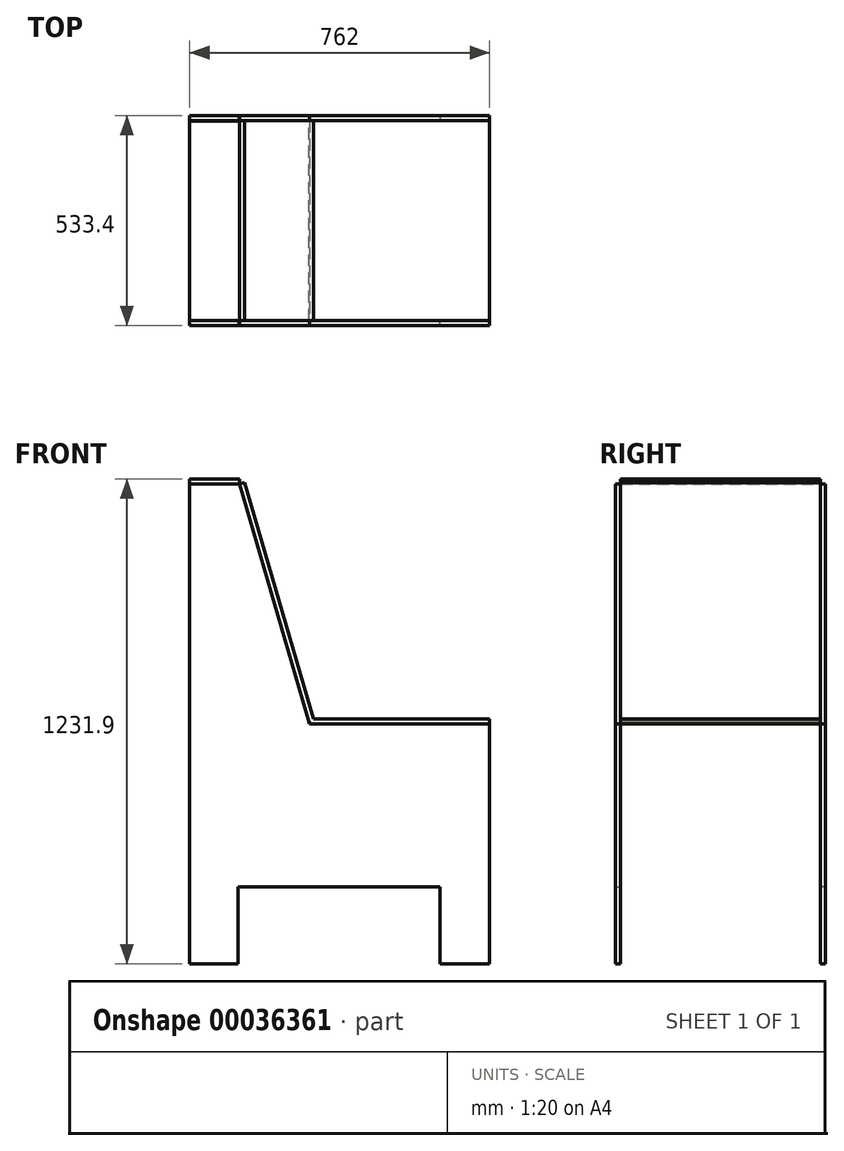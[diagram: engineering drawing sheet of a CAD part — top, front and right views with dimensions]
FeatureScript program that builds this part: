
annotation { "Feature Type Name" : "Feature", "Feature Type Description" : "" }
export const myFeature = defineFeature(function(context is Context, id is Id, definition is map)
    precondition{}
    {
        {
            var Q0;
            Q0=qCreatedBy(makeId("Front.planeOp"),FACE);
            var sketch = newSketch(context, id + "F0", { "sketchPlane" : qUnion([Q0])});
            skLineSegment(sketch, "E0", {"start": v(98.48, 576.75) * mm, "end": v(98.48, -642.45) * mm});
            skLineSegment(sketch, "E1", {"start": v(98.48, 576.75) * mm, "end": v(225.48, 576.75) * mm});
            skLineSegment(sketch, "E2", {"start": v(225.48, 576.75) * mm, "end": v(403.28, -32.85) * mm});
            skLineSegment(sketch, "E3", {"start": v(403.28, -32.85) * mm, "end": v(860.48, -32.85) * mm});
            skLineSegment(sketch, "E4", {"start": v(98.48, -642.45) * mm, "end": v(860.48, -642.45) * mm});
            skLineSegment(sketch, "E5", {"start": v(860.48, -32.85) * mm, "end": v(860.48, -642.45) * mm});
            skSolve(sketch);
        }
        {
            var Q0;
            Q0=makeQuery(id+"F0.imprint","IMPRINT",FACE,{"disambiguationData":[TD([[makeQuery(id+"F0.imprint","IMPRINT",EDGE,{"derivedFrom":sQuery(id+"F0.wireOp",EDGE,"E0")}),1.0]])]});
            extrude(context, id + "F1", {"entities" : qUnion([Q0]), "oppositeDirection" : true, "depth" : 12.7 * mm});
        }
        {
            var Q0;
            Q0=makeQuery(id+"F1.opExtrude","CAP_FACE",FACE,{"disambiguationData":[OSD([sQuery(id+"F0.wireOp",EDGE,"E0"),sQuery(id+"F0.wireOp",EDGE,"E1"),sQuery(id+"F0.wireOp",EDGE,"E2"),sQuery(id+"F0.wireOp",EDGE,"E3"),sQuery(id+"F0.wireOp",EDGE,"E4"),sQuery(id+"F0.wireOp",EDGE,"E5")])],"isStart":true});
            var sketch = newSketch(context, id + "F2", { "sketchPlane" : qUnion([Q0])});
            skLineSegment(sketch, "E6.bottom", {"start": v(221.16, -446.46) * mm, "end": v(733.7, -446.46) * mm});
            skLineSegment(sketch, "E6.top", {"start": v(221.16, -642.45) * mm, "end": v(733.7, -642.45) * mm});
            skLineSegment(sketch, "E6.left", {"start": v(221.16, -446.46) * mm, "end": v(221.16, -642.45) * mm});
            skLineSegment(sketch, "E6.right", {"start": v(733.7, -446.46) * mm, "end": v(733.7, -642.45) * mm});
            skSolve(sketch);
        }
        {
            var Q0;
            Q0=makeQuery(id+"F2.imprint","IMPRINT",FACE,{"disambiguationData":[TD([[makeQuery(id+"F2.imprint","IMPRINT",EDGE,{"derivedFrom":sQuery(id+"F2.wireOp",EDGE,"E6.bottom")}),-1.0]])]});
            extrude(context, id + "F3", {"entities" : qUnion([Q0]), "operationType" : NewBodyOperationType.REMOVE, "endBound" : BoundingType.THROUGH_ALL, "oppositeDirection" : true, "depth" : 12.7 * mm});
        }
        {
            var Q0;
            Q0=makeQuery(id+"F1.opExtrude","CAP_FACE",FACE,{"disambiguationData":[OSD([sQuery(id+"F0.wireOp",EDGE,"E0"),sQuery(id+"F0.wireOp",EDGE,"E1"),sQuery(id+"F0.wireOp",EDGE,"E2"),sQuery(id+"F0.wireOp",EDGE,"E3"),sQuery(id+"F0.wireOp",EDGE,"E4"),sQuery(id+"F0.wireOp",EDGE,"E5")])],"isStart":true});
            var sketch = newSketch(context, id + "F4", { "sketchPlane" : qUnion([Q0])});
            skLineSegment(sketch, "E7.0", {"start": v(98.48, 576.75) * mm, "end": v(225.48, 576.75) * mm});
            skLineSegment(sketch, "E8.0", {"start": v(225.48, 576.75) * mm, "end": v(403.28, -32.85) * mm});
            skLineSegment(sketch, "E9.0", {"start": v(403.28, -32.85) * mm, "end": v(860.48, -32.85) * mm});
            skLineSegment(sketch, "E10.0", {"start": v(860.48, -32.85) * mm, "end": v(860.48, -642.45) * mm});
            skLineSegment(sketch, "E11.0", {"start": v(733.7, -642.45) * mm, "end": v(860.48, -642.45) * mm});
            skLineSegment(sketch, "E12.0", {"start": v(733.7, -446.46) * mm, "end": v(733.7, -642.45) * mm});
            skLineSegment(sketch, "E13.0", {"start": v(221.16, -446.46) * mm, "end": v(733.7, -446.46) * mm});
            skLineSegment(sketch, "E14.0", {"start": v(221.16, -446.46) * mm, "end": v(221.16, -642.45) * mm});
            skLineSegment(sketch, "E15.0", {"start": v(98.48, -642.45) * mm, "end": v(221.16, -642.45) * mm});
            skLineSegment(sketch, "E16.0", {"start": v(98.48, 576.75) * mm, "end": v(98.48, -642.45) * mm});
            skSolve(sketch);
        }
        {
            var Q0;
            Q0=makeQuery(id+"F4.imprint","IMPRINT",FACE,{"disambiguationData":[TD([[makeQuery(id+"F4.imprint","IMPRINT",EDGE,{"derivedFrom":sQuery(id+"F4.wireOp",EDGE,"E7.0")}),-1.0]])]});
            cPlane(context, id + "F5", {"entities" : qUnion([Q0]), "cplaneType" : CPlaneType.OFFSET, "offset" : 508 * mm, "width" : 152.4 * mm, "height" : 152.4 * mm});
        }
        {
            var Q0;
            Q0=qCreatedBy(id+"F5.planeOp",FACE);
            var sketch = newSketch(context, id + "F6", { "sketchPlane" : qUnion([Q0])});
            skLineSegment(sketch, "E17.0", {"start": v(225.48, 576.75) * mm, "end": v(403.28, -32.85) * mm});
            skLineSegment(sketch, "E18.0", {"start": v(403.28, -32.85) * mm, "end": v(860.48, -32.85) * mm});
            skLineSegment(sketch, "E19.0", {"start": v(860.48, -32.85) * mm, "end": v(860.48, -642.45) * mm});
            skLineSegment(sketch, "E20.0", {"start": v(733.7, -642.45) * mm, "end": v(860.48, -642.45) * mm});
            skLineSegment(sketch, "E21.0", {"start": v(733.7, -446.46) * mm, "end": v(733.7, -642.45) * mm});
            skLineSegment(sketch, "E22.0", {"start": v(221.16, -446.46) * mm, "end": v(733.7, -446.46) * mm});
            skLineSegment(sketch, "E23.0", {"start": v(221.16, -446.46) * mm, "end": v(221.16, -642.45) * mm});
            skLineSegment(sketch, "E24.0", {"start": v(98.48, -642.45) * mm, "end": v(221.16, -642.45) * mm});
            skLineSegment(sketch, "E25.0", {"start": v(98.48, 576.75) * mm, "end": v(98.48, -642.45) * mm});
            skLineSegment(sketch, "E26.0", {"start": v(98.48, 576.75) * mm, "end": v(225.48, 576.75) * mm});
            skSolve(sketch);
        }
        {
            var Q0;
            Q0=makeQuery(id+"F6.imprint","IMPRINT",FACE,{"disambiguationData":[TD([[makeQuery(id+"F6.imprint","IMPRINT",EDGE,{"derivedFrom":sQuery(id+"F6.wireOp",EDGE,"E17.0")}),-1.0]])]});
            extrude(context, id + "F7", {"entities" : qUnion([Q0]), "depth" : 12.7 * mm});
        }
        {
            var Q0;
            Q0=makeQuery(id+"F7.opExtrude","SWEPT_FACE",FACE,{"disambiguationData":[OSD([sQuery(id+"F6.wireOp",EDGE,"E18.0")])]});
            var sketch = newSketch(context, id + "F8", { "sketchPlane" : qUnion([Q0])});
            skLineSegment(sketch, "E27.0.0", {"start": v(98.48, 0) * mm, "end": v(225.48, 0) * mm});
            skLineSegment(sketch, "E27.0.1", {"start": v(225.48, 0) * mm, "end": v(225.48, 12.7) * mm});
            skLineSegment(sketch, "E27.0.2", {"start": v(225.48, 12.7) * mm, "end": v(98.48, 12.7) * mm});
            skLineSegment(sketch, "E27.0.3", {"start": v(98.48, 12.7) * mm, "end": v(98.48, 0) * mm});
            skLineSegment(sketch, "E28.0.0", {"start": v(403.28, 0) * mm, "end": v(860.48, 0) * mm});
            skLineSegment(sketch, "E28.0.1", {"start": v(860.48, 0) * mm, "end": v(860.48, 12.7) * mm});
            skLineSegment(sketch, "E28.0.2", {"start": v(860.48, 12.7) * mm, "end": v(403.28, 12.7) * mm});
            skLineSegment(sketch, "E28.0.3", {"start": v(403.28, 12.7) * mm, "end": v(403.28, 0) * mm});
            skLineSegment(sketch, "E29.0.0", {"start": v(860.48, -508) * mm, "end": v(403.28, -508) * mm});
            skLineSegment(sketch, "E29.0.1", {"start": v(403.28, -508) * mm, "end": v(403.28, -520.7) * mm});
            skLineSegment(sketch, "E29.0.2", {"start": v(403.28, -520.7) * mm, "end": v(860.48, -520.7) * mm});
            skLineSegment(sketch, "E29.0.3", {"start": v(860.48, -520.7) * mm, "end": v(860.48, -508) * mm});
            skLineSegment(sketch, "E30.0.0", {"start": v(403.28, -508) * mm, "end": v(225.48, -508) * mm});
            skLineSegment(sketch, "E30.0.1", {"start": v(225.48, -508) * mm, "end": v(225.48, -520.7) * mm});
            skLineSegment(sketch, "E30.0.2", {"start": v(225.48, -520.7) * mm, "end": v(403.28, -520.7) * mm});
            skLineSegment(sketch, "E30.0.3", {"start": v(403.28, -520.7) * mm, "end": v(403.28, -508) * mm});
            skLineSegment(sketch, "E31.0.0", {"start": v(225.48, -508) * mm, "end": v(98.48, -508) * mm});
            skLineSegment(sketch, "E31.0.1", {"start": v(98.48, -508) * mm, "end": v(98.48, -520.7) * mm});
            skLineSegment(sketch, "E31.0.2", {"start": v(98.48, -520.7) * mm, "end": v(225.48, -520.7) * mm});
            skLineSegment(sketch, "E31.0.3", {"start": v(225.48, -520.7) * mm, "end": v(225.48, -508) * mm});
            skLineSegment(sketch, "E32.bottom", {"start": v(403.28, 12.7) * mm, "end": v(860.48, 12.7) * mm});
            skLineSegment(sketch, "E32.top", {"start": v(403.28, -508) * mm, "end": v(860.48, -508) * mm});
            skLineSegment(sketch, "E32.left", {"start": v(403.28, 12.7) * mm, "end": v(403.28, -508) * mm});
            skLineSegment(sketch, "E32.right", {"start": v(860.48, 12.7) * mm, "end": v(860.48, -508) * mm});
            skSolve(sketch);
        }
        {
            var Q0;
            {var subQ1=sQuery(id+"F8.wireOp",EDGE,"E28.0.0");Q0=makeQuery(id+"F8.imprint","IMPRINT",FACE,{"disambiguationData":[TD([[makeQuery(id+"F8.imprint","IMPRINT",EDGE,{"derivedFrom":subQ1}),-1.0]])]});}
            extrude(context, id + "F9", {"entities" : qUnion([Q0]), "depth" : 12.7 * mm});
        }
        {
            var Q0;
            Q0=makeQuery(id+"F7.opExtrude","SWEPT_FACE",FACE,{"disambiguationData":[OSD([sQuery(id+"F6.wireOp",EDGE,"E17.0")])]});
            var sketch = newSketch(context, id + "F10", { "sketchPlane" : qUnion([Q0])});
            skLineSegment(sketch, "E33.bottom", {"start": v(-508, 490.55) * mm, "end": v(0, 490.55) * mm});
            skLineSegment(sketch, "E33.top", {"start": v(-508, -138.25) * mm, "end": v(0, -138.25) * mm});
            skLineSegment(sketch, "E33.left", {"start": v(-508, 490.55) * mm, "end": v(-508, -138.25) * mm});
            skLineSegment(sketch, "E33.right", {"start": v(0, 490.55) * mm, "end": v(0, -138.25) * mm});
            skSolve(sketch);
        }
        {
            var Q0;
            Q0=makeQuery(id+"F10.imprint","IMPRINT",FACE,{"disambiguationData":[TD([[makeQuery(id+"F10.imprint","IMPRINT",EDGE,{"derivedFrom":sQuery(id+"F10.wireOp",EDGE,"E33.bottom")}),-1.0]])]});
            extrude(context, id + "F11", {"entities" : qUnion([Q0]), "operationType" : NewBodyOperationType.ADD, "depth" : 12.7 * mm});
        }
        {
            var Q0;
            Q0=makeQuery(id+"F7.opExtrude","SWEPT_FACE",FACE,{"disambiguationData":[OSD([sQuery(id+"F6.wireOp",EDGE,"E26.0")])]});
            var sketch = newSketch(context, id + "F12", { "sketchPlane" : qUnion([Q0])});
            skLineSegment(sketch, "E34.bottom", {"start": v(225.27, -1.08) * mm, "end": v(98.48, -1.08) * mm});
            skLineSegment(sketch, "E34.top", {"start": v(225.27, -508) * mm, "end": v(98.48, -508) * mm});
            skLineSegment(sketch, "E34.left", {"start": v(225.27, -1.08) * mm, "end": v(225.27, -508) * mm});
            skLineSegment(sketch, "E34.right", {"start": v(98.48, -1.08) * mm, "end": v(98.48, -508) * mm});
            skSolve(sketch);
        }
        {
            var Q0;
            Q0=makeQuery(id+"F12.imprint","IMPRINT",FACE,{"disambiguationData":[TD([[makeQuery(id+"F12.imprint","IMPRINT",EDGE,{"derivedFrom":sQuery(id+"F12.wireOp",EDGE,"E34.bottom")}),1.0]])]});
            extrude(context, id + "F13", {"entities" : qUnion([Q0]), "depth" : 12.7 * mm});
        }
    });
